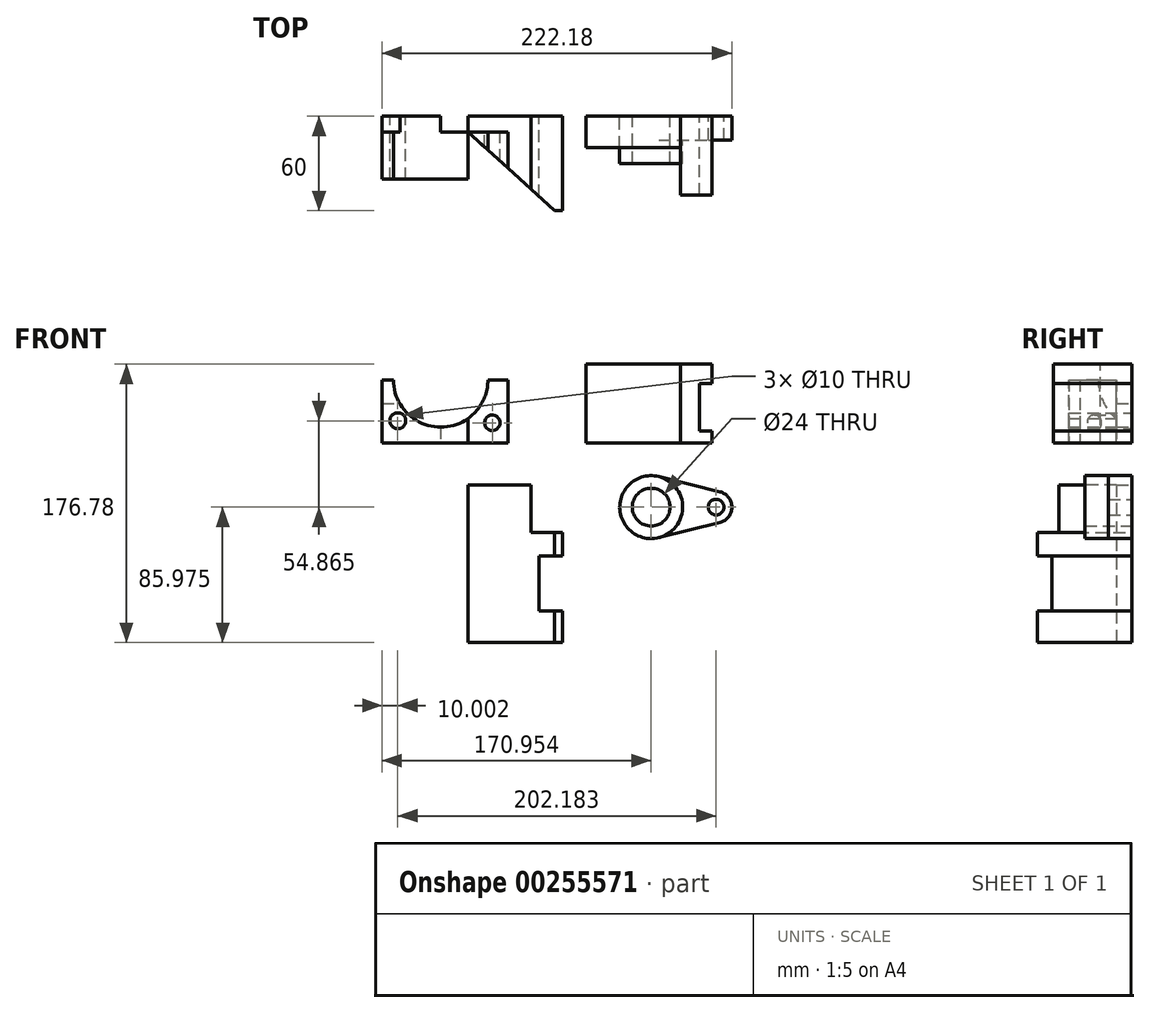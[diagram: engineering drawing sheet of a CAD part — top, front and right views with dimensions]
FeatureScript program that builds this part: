
annotation { "Feature Type Name" : "Feature", "Feature Type Description" : "" }
export const myFeature = defineFeature(function(context is Context, id is Id, definition is map)
    precondition{}
    {
        {
            var Q0;
            Q0=qCreatedBy(makeId("Front.planeOp"),FACE);
            var sketch = newSketch(context, id + "F0", { "sketchPlane" : qUnion([Q0])});
            skLineSegment(sketch, "E0.bottom", {"start": v(0, 0) * mm, "end": v(80, 0) * mm});
            skLineSegment(sketch, "E0.top", {"start": v(0, 50) * mm, "end": v(80, 50) * mm});
            skLineSegment(sketch, "E0.left", {"start": v(0, 0) * mm, "end": v(0, 50) * mm});
            skLineSegment(sketch, "E0.right", {"start": v(80, 0) * mm, "end": v(80, 50) * mm});
            skLineSegment(sketch, "E1", {"start": v(60, 50) * mm, "end": v(60, 0) * mm});
            skLineSegment(sketch, "E2.bottom", {"start": v(80, 37.59) * mm, "end": v(72, 37.59) * mm});
            skLineSegment(sketch, "E2.top", {"start": v(80, 7.59) * mm, "end": v(72, 7.59) * mm});
            skLineSegment(sketch, "E2.left", {"start": v(80, 37.59) * mm, "end": v(80, 7.59) * mm});
            skLineSegment(sketch, "E2.right", {"start": v(72, 37.59) * mm, "end": v(72, 7.59) * mm});
            skSolve(sketch);
        }
        {
            var Q0;
            {var subQ0=sQuery(id+"F0.wireOp",EDGE,"E0.left");Q0=makeQuery(id+"F0.imprint","IMPRINT",FACE,{"disambiguationData":[TD([[makeQuery(id+"F0.imprint","IMPRINT",EDGE,{"derivedFrom":subQ0}),-1.0]])]});}
            extrude(context, id + "F1", {"entities" : qUnion([Q0]), "depth" : 20 * mm});
        }
        {
            var Q0;
            {var subQ8=sQuery(id+"F0.wireOp",EDGE,"E1");Q0=makeQuery(id+"F0.imprint","IMPRINT",FACE,{"disambiguationData":[TD([[makeQuery(id+"F0.imprint","IMPRINT",EDGE,{"derivedFrom":subQ8}),1.0]])]});}
            extrude(context, id + "F2", {"entities" : qUnion([Q0]), "depth" : 50 * mm});
        }
        {
            var Q0;
            Q0=qCreatedBy(makeId("Front.planeOp"),FACE);
            var sketch = newSketch(context, id + "F3", { "sketchPlane" : qUnion([Q0])});
            skCircle(sketch, "E3", {"center": v(41.5, -40.8) * mm, "radius": 12 * mm});
            skCircle(sketch, "E4", {"center": v(41.5, -40.8) * mm, "radius": 20 * mm});
            skCircle(sketch, "E5", {"center": v(82.72, -40.8) * mm, "radius": 5 * mm});
            skArc(sketch, "E6", {"start": v(85.15, -50.5) * mm, "mid": v(92.72, -40.8) * mm, "end": v(85.15, -31.1) * mm});
            skLineSegment(sketch, "E7", {"start": v(46.34, -21.4) * mm, "end": v(85.15, -31.1) * mm});
            skLineSegment(sketch, "E8", {"start": v(46.34, -60.2) * mm, "end": v(85.15, -50.5) * mm});
            skSolve(sketch);
        }
        {
            var Q0;
            Q0=makeQuery(id+"F3.imprint","IMPRINT",FACE,{"disambiguationData":[TD([[makeQuery(id+"F3.imprint","IMPRINT",EDGE,{"derivedFrom":sQuery(id+"F3.wireOp",EDGE,"E3")}),-1.0]])]});
            extrude(context, id + "F4", {"entities" : qUnion([Q0]), "depth" : 30 * mm});
        }
        {
            var Q0;
            Q0=makeQuery(id+"F3.imprint","IMPRINT",FACE,{"disambiguationData":[TD([[makeQuery(id+"F3.imprint","IMPRINT",EDGE,{"derivedFrom":sQuery(id+"F3.wireOp",EDGE,"E5")}),-1.0]])]});
            extrude(context, id + "F5", {"entities" : qUnion([Q0]), "operationType" : NewBodyOperationType.ADD, "depth" : 15 * mm});
        }
        {
            var Q0;
            Q0=qCreatedBy(makeId("Front.planeOp"),FACE);
            var sketch = newSketch(context, id + "F6", { "sketchPlane" : qUnion([Q0])});
            skLineSegment(sketch, "E9.bottom", {"start": v(-49.46, 0) * mm, "end": v(-129.46, 0) * mm});
            skLineSegment(sketch, "E9.top", {"start": v(-49.46, 40) * mm, "end": v(-129.46, 40) * mm});
            skLineSegment(sketch, "E9.left", {"start": v(-49.46, 0) * mm, "end": v(-49.46, 40) * mm});
            skLineSegment(sketch, "E9.right", {"start": v(-129.46, 0) * mm, "end": v(-129.46, 40) * mm});
            skArc(sketch, "E10", {"start": v(-122.2, 40) * mm, "mid": v(-92.2, 10) * mm, "end": v(-62.2, 40) * mm});
            skCircle(sketch, "E11", {"center": v(-119.46, 14.06) * mm, "radius": 5 * mm});
            skCircle(sketch, "E12", {"center": v(-59.46, 12.75) * mm, "radius": 5 * mm});
            skLineSegment(sketch, "E13", {"start": v(-129.46, 25) * mm, "end": v(-118.19, 25) * mm});
            skLineSegment(sketch, "E14.bottom", {"start": v(-92.2, 40) * mm, "end": v(-49.46, 40) * mm});
            skLineSegment(sketch, "E14.top", {"start": v(-92.2, 0) * mm, "end": v(-49.46, 0) * mm});
            skLineSegment(sketch, "E14.left", {"start": v(-92.2, 40) * mm, "end": v(-92.2, 0) * mm});
            skLineSegment(sketch, "E14.right", {"start": v(-49.46, 40) * mm, "end": v(-49.46, 0) * mm});
            skSolve(sketch);
        }
        {
            var Q0;
            {var subQ5=sQuery(id+"F6.wireOp",EDGE,"E13");Q0=makeQuery(id+"F6.imprint","IMPRINT",FACE,{"disambiguationData":[TD([[makeQuery(id+"F6.imprint","IMPRINT",EDGE,{"derivedFrom":subQ5}),1.0]])]});}
            var Q1;
            {var subQ5=sQuery(id+"F6.wireOp",EDGE,"E9.bottom");Q1=makeQuery(id+"F6.imprint","IMPRINT",FACE,{"disambiguationData":[TD([[makeQuery(id+"F6.imprint","IMPRINT",EDGE,{"derivedFrom":subQ5}),-1.0]])]});}
            var Q2;
            Q2=makeQuery(id+"F6.imprint","IMPRINT",FACE,{"disambiguationData":[TD([[makeQuery(id+"F6.imprint","IMPRINT",EDGE,{"derivedFrom":sQuery(id+"F6.wireOp",EDGE,"E12")}),-1.0]])]});
            extrude(context, id + "F7", {"entities" : qUnion([Q0, Q1, Q2]), "depth" : 40 * mm});
        }
        {
            var Q0;
            {var subQ5=sQuery(id+"F6.wireOp",EDGE,"E13");Q0=makeQuery(id+"F6.imprint","IMPRINT",FACE,{"disambiguationData":[TD([[makeQuery(id+"F6.imprint","IMPRINT",EDGE,{"derivedFrom":subQ5}),1.0]])]});}
            var Q1;
            Q1=makeQuery(id+"F6.imprint","IMPRINT",FACE,{"disambiguationData":[TD([[makeQuery(id+"F6.imprint","IMPRINT",EDGE,{"derivedFrom":sQuery(id+"F6.wireOp",EDGE,"E12")}),-1.0]])]});
            extrude(context, id + "F8", {"entities" : qUnion([Q0, Q1]), "operationType" : NewBodyOperationType.REMOVE, "depth" : 10 * mm});
        }
        {
            var Q0;
            Q0=qCreatedBy(makeId("Front.planeOp"),FACE);
            var sketch = newSketch(context, id + "F9", { "sketchPlane" : qUnion([Q0])});
            skLineSegment(sketch, "E15", {"start": v(-74.85, -126.78) * mm, "end": v(-14.85, -126.78) * mm});
            skLineSegment(sketch, "E16", {"start": v(-14.85, -126.78) * mm, "end": v(-14.85, -106.78) * mm});
            skLineSegment(sketch, "E17", {"start": v(-14.85, -106.78) * mm, "end": v(-29.85, -106.78) * mm});
            skLineSegment(sketch, "E18", {"start": v(-29.85, -106.78) * mm, "end": v(-29.85, -71.78) * mm});
            skLineSegment(sketch, "E19", {"start": v(-29.85, -71.78) * mm, "end": v(-14.85, -71.78) * mm});
            skLineSegment(sketch, "E20", {"start": v(-14.85, -71.78) * mm, "end": v(-14.85, -56.78) * mm});
            skLineSegment(sketch, "E21", {"start": v(-14.85, -56.78) * mm, "end": v(-34.85, -56.78) * mm});
            skLineSegment(sketch, "E22", {"start": v(-34.85, -56.78) * mm, "end": v(-34.85, -26.78) * mm});
            skLineSegment(sketch, "E23", {"start": v(-34.85, -26.78) * mm, "end": v(-74.85, -26.78) * mm});
            skLineSegment(sketch, "E24", {"start": v(-74.85, -26.78) * mm, "end": v(-74.85, -126.78) * mm});
            skSolve(sketch);
        }
        {
            var Q0;
            Q0=makeQuery(id+"F9.imprint","IMPRINT",FACE,{"disambiguationData":[TD([[makeQuery(id+"F9.imprint","IMPRINT",EDGE,{"derivedFrom":sQuery(id+"F9.wireOp",EDGE,"E15")}),1.0]])]});
            extrude(context, id + "F10", {"entities" : qUnion([Q0]), "depth" : 60 * mm});
        }
        {
            var Q0;
            Q0=makeQuery(id+"F10.opExtrude","SWEPT_FACE",FACE,{"disambiguationData":[OSD([sQuery(id+"F9.wireOp",EDGE,"E15")])]});
            var sketch = newSketch(context, id + "F11", { "sketchPlane" : qUnion([Q0])});
            skLineSegment(sketch, "E25", {"start": v(-74.85, 10) * mm, "end": v(-19.85, 60) * mm});
            skLineSegment(sketch, "E26", {"start": v(-74.85, 0) * mm, "end": v(-74.85, 10) * mm});
            skLineSegment(sketch, "E27", {"start": v(-19.85, 60) * mm, "end": v(-14.85, 60) * mm});
            skLineSegment(sketch, "E28", {"start": v(-74.85, 10) * mm, "end": v(-74.85, 60) * mm});
            skLineSegment(sketch, "E29", {"start": v(-74.85, 60) * mm, "end": v(-19.85, 60) * mm});
            skSolve(sketch);
        }
        {
            var Q0;
            Q0 = qSketchRegion(id + "F11", true);
            extrude(context, id + "F12", {"entities" : qUnion([Q0]), "operationType" : NewBodyOperationType.REMOVE, "endBound" : BoundingType.THROUGH_ALL, "oppositeDirection" : true, "depth" : 25 * mm});
        }
    });
